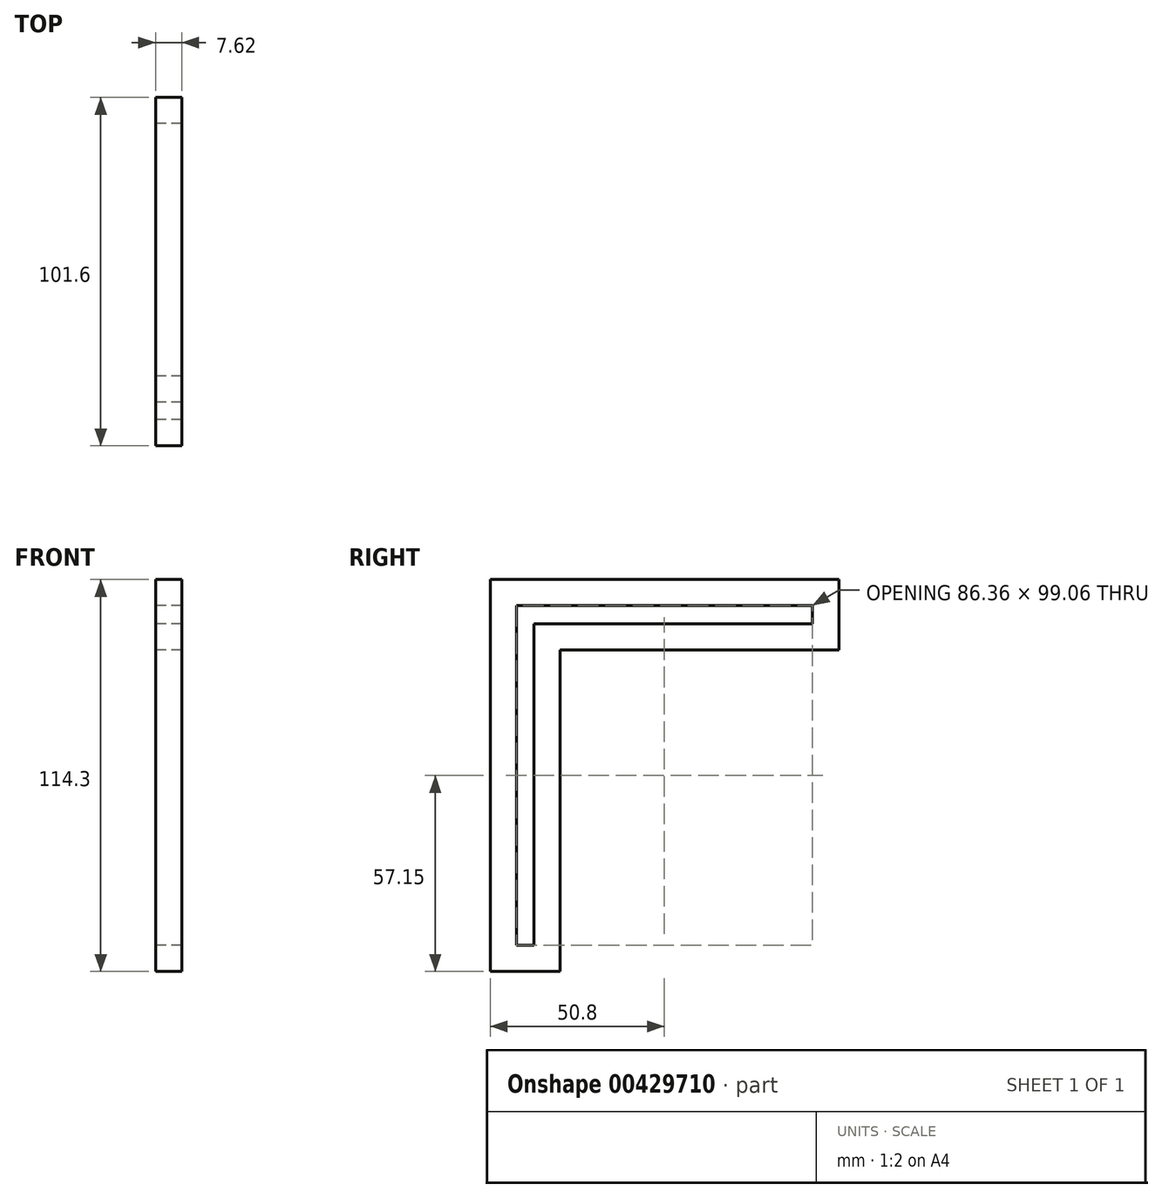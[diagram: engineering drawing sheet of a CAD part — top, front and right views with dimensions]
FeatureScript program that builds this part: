
annotation { "Feature Type Name" : "Feature", "Feature Type Description" : "" }
export const myFeature = defineFeature(function(context is Context, id is Id, definition is map)
    precondition{}
    {
        {
            var Q0;
            Q0=qCreatedBy(makeId("Right.planeOp"),FACE);
            var sketch = newSketch(context, id + "F0", { "sketchPlane" : qUnion([Q0])});
            skLineSegment(sketch, "E0.bottom", {"start": v(0, -114.3) * mm, "end": v(20.32, -114.3) * mm});
            skLineSegment(sketch, "E0.top", {"start": v(0, 0) * mm, "end": v(20.32, 0) * mm});
            skLineSegment(sketch, "E0.left", {"start": v(0, -114.3) * mm, "end": v(0, 0) * mm});
            skLineSegment(sketch, "E0.right", {"start": v(20.32, -114.3) * mm, "end": v(20.32, -20.57) * mm});
            skLineSegment(sketch, "E1.bottom", {"start": v(0, 0) * mm, "end": v(101.6, 0) * mm});
            skLineSegment(sketch, "E1.top", {"start": v(20.32, -20.57) * mm, "end": v(101.6, -20.57) * mm});
            skLineSegment(sketch, "E1.right", {"start": v(101.6, 0) * mm, "end": v(101.6, -20.57) * mm});
            skLineSegment(sketch, "E2", {"start": v(7.62, -106.68) * mm, "end": v(7.62, -7.62) * mm});
            skLineSegment(sketch, "E3", {"start": v(7.62, -7.62) * mm, "end": v(93.98, -7.62) * mm});
            skLineSegment(sketch, "E4", {"start": v(93.98, -7.62) * mm, "end": v(93.98, -12.95) * mm});
            skLineSegment(sketch, "E5", {"start": v(93.98, -12.95) * mm, "end": v(12.7, -12.95) * mm});
            skLineSegment(sketch, "E6", {"start": v(12.7, -12.95) * mm, "end": v(12.7, -106.68) * mm});
            skLineSegment(sketch, "E7", {"start": v(12.7, -106.68) * mm, "end": v(7.62, -106.68) * mm});
            skSolve(sketch);
        }
        {
            var Q0;
            Q0=makeQuery(id+"F0.imprint","IMPRINT",FACE,{"disambiguationData":[TD([[makeQuery(id+"F0.imprint","IMPRINT",EDGE,{"derivedFrom":sQuery(id+"F0.wireOp",EDGE,"E0.bottom")}),1.0]])]});
            extrude(context, id + "F1", {"entities" : qUnion([Q0]), "depth" : 7.62 * mm});
        }
    });
